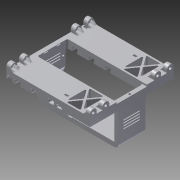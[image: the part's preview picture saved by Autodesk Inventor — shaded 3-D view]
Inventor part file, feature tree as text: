
AUTODESK INVENTOR PART (.ipt)
format: ipt  version: 2015 (Build 190159000, 159)  size: 907,264 bytes
history: native  units: mm
features: sketch x22, extrude x18, hole x5, plane x5, projected_geometry x5, reference x5, mirror x4, fillet x2, other x1, pattern_linear x1
ambient origin geometry x8: Origin, YZ Plane, XZ Plane, XY Plane, X Axis, Y Axis, Z Axis, Center Point
bodies: Body1 (feature_tree), Body2 (feature_tree), Body3 (feature_tree), Body4 (feature_tree), Body5 (feature_tree), Body6 (feature_tree), Body7 (feature_tree), Body8 (feature_tree), Body9 (feature_tree), Body10 (feature_tree), Body11 (feature_tree), Body12 (feature_tree), Body13 (feature_tree), Body14 (feature_tree), Body15 (feature_tree)
feature tree (68):
  other  "Sólido1"
  extrude  "Extrusión1"  Depth=36.0mm
  sketch  "Boceto5"  dims[d6=100.0mm d7=100.0mm d8=0.0mm]
  sketch  "Boceto6"  dims[d26=0.1mm d27=0.1mm]
  extrude  "Extrusión4"  Depth=100.0mm TaperAngle=0.0deg
  extrude  "Extrusión5"  Depth=0.1mm
  hole  "Agujero2"  [1 undecoded]
  extrude  "Extrusión6"  Depth=0.1mm
  extrude  "Extrusión7"  Depth=20.0mm TaperAngle=0.0deg
  extrude  "Extrusión8"  Depth=20.0mm TaperAngle=0.0deg
  fillet  "Empalme2"  Radius=2.0mm
  hole  "Agujero3"  [1 undecoded]
  sketch  "Boceto13"  dims[d51=5.0mm d52=20.0mm d53=0.0mm d54=2.0mm]
  plane  "Plano de trabajo2"
  extrude  "Extrusión9"  Depth=100.0mm TaperAngle=0.0deg
  mirror  "Simetría2"
  extrude  "Extrusión10"  Depth=5.0mm
  extrude  "Extrusión11"  Depth=10.0mm
  extrude  "Extrusión12"  Depth=5.0mm
  hole  "Agujero4"  [1 undecoded]
  sketch  "Boceto18"  dims[d65=5.0mm d66=2.5mm]
  plane  "Plano de trabajo4"
  extrude  "Extrusión13"  Depth=45.0mm
  extrude  "Extrusión14"  Depth=25.0mm
  sketch  "Boceto20"  dims[d69=2.5mm d70=45.0mm]
  plane  "Plano de trabajo5"
  extrude  "Extrusión15"  Depth=35.0mm
  sketch  "Boceto22"  dims[d73=2.5mm d74=35.0mm]
  extrude  "Extrusión17"  Depth=4.2mm
  extrude  "Extrusión16"  [1 undecoded]
  fillet  "Empalme3"  Radius=10.0mm
  pattern_linear  "Patrón rectangular1"  Count1=2  [1 undecoded]
  mirror  "Simetría3"
  mirror  "Simetría4"
  extrude  "Extrusión18"  Depth=1.0mm
  mirror  "Simetría5"
  sketch  "Boceto24"  dims[d83=4.2mm d84=-8.0mm d85=-2.2mm d86=10.0mm d87=0.0mm]
  sketch  "Boceto25"  dims[d88=1.0mm d89=20.0mm]
  hole  "Agujero5"  [1 undecoded]
  hole  "Agujero6"  [1 undecoded]
  extrude  "Extrusión19"  Depth=1.0mm
  extrude  "Extrusión20"  Depth=50.0mm TaperAngle=0.0deg
  sketch  "Boceto1"  dims[d1=8.0mm d5=36.0mm]
  sketch  "Boceto7"  dims[d28=0.1mm d29=3.0mm d30=0.0mm]
  sketch  "Boceto8"  dims[d31=0.1mm d32=0.1mm]
  projected_geometry  "Contorno proyectado1"
  sketch  "Boceto9"  dims[d33=3.1mm d34=0.0mm]
  sketch  "Boceto11"  dims[d35=2.3mm d36=6.0mm d37=4.0mm d38=2.0mm d39=90.0deg d40=20.0mm d41=20.594885mm d44=3.1mm d45=0.0mm]
  projected_geometry  "Contorno proyectado2"
  projected_geometry  "Contorno proyectado3"
  plane  "Plano de trabajo1"
  sketch  "Boceto14"  dims[d55=5.0mm d56=15.0mm d57=2.0mm]
  sketch  "Boceto15"  dims[d58=2.0mm d59=100.0mm d60=0.0mm]
  sketch  "Boceto16"  dims[d61=2.5mm d62=5.0mm]
  projected_geometry  "Contorno proyectado6"
  sketch  "Boceto17"  dims[d63=10.0mm d64=2.5mm]
  projected_geometry  "Contorno proyectado7"
  plane  "Plano de trabajo3"
  sketch  "Boceto19"  dims[d67=2.5mm d68=15.0mm]
  sketch  "Boceto21"  dims[d71=2.5mm d72=25.0mm]
  sketch  "Boceto23"  dims[d75=2.2mm d76=6.0mm d77=4.0mm d78=2.0mm d79=90.0deg d80=8.0mm d81=20.594885mm d82=4.2mm]
  reference  "Referencia10"
  reference  "Referencia11"
  reference  "Referencia12"
  reference  "Referencia13"
  sketch  "Boceto28"  dims[d90=1.0mm d91=20.0mm d92=1.0mm d93=20.0mm]
  sketch  "Boceto29"  dims[d94=1.0mm d95=20.0mm d96=2.0mm d97=2.0mm d98=2.0mm d99=1.0mm d100=50.0mm d101=0.0mm d102=20.0mm d103=1.0mm d104=20.0mm d105=1.0mm d106=20.0mm d107=1.0mm d108=2.0mm d109=2.0mm d110=0.5mm d111=10.0mm d112=50.0mm d113=0.0mm d114=2.0mm d115=0.0mm d116=90.0deg d117=2.4mm d118=6.0mm d119=4.0mm d120=2.0mm d121=90.0deg d122=15.0mm d123=20.594885mm d125=-8.0mm d126=-2.2mm d127=1.0mm d128=0.0mm d130=5.0mm d131=1.0mm d132=5.0mm d133=1.0mm d134=10.0mm d135=0.5mm d136=47.0mm d137=0.0mm d138=3.4mm d139=6.0mm d140=-5.0mm d141=47.0mm d142=0.0mm d143=5.7mm d144=10.0mm d145=0.0mm d146=4.0mm d147=20.0mm d149=15.0mm d150=3.0mm d151=45.0deg d152=2.5mm d153=0.0mm d154=3.0mm d155=0.0mm d156=2.0mm d157=24.0mm d158=2.0mm d159=1.0mm d160=1.0mm d161=1.0mm d162=1.0mm d163=1.0mm d164=10.0mm d165=0.0mm d166=2.0mm d167=2.4mm d168=6.0mm d169=4.0mm d170=2.0mm d171=90.0deg d172=8.0mm d173=20.594885mm d174=2.4mm d175=6.0mm d176=4.0mm d177=2.0mm d178=90.0deg d179=8.0mm d180=20.594885mm d181=4.2mm d182=4.2mm d183=3.0mm d184=0.0mm d185=4.2mm d186=4.2mm d187=3.0mm d188=0.0mm d189=0.1mm d190=0.1mm]
  reference  "Referencia14"
note: 7 required parameter values undecoded (feature->parameter linkage not recoverable at this tier; creation-order binding heuristic only, values carry confidence <= 0.55)
